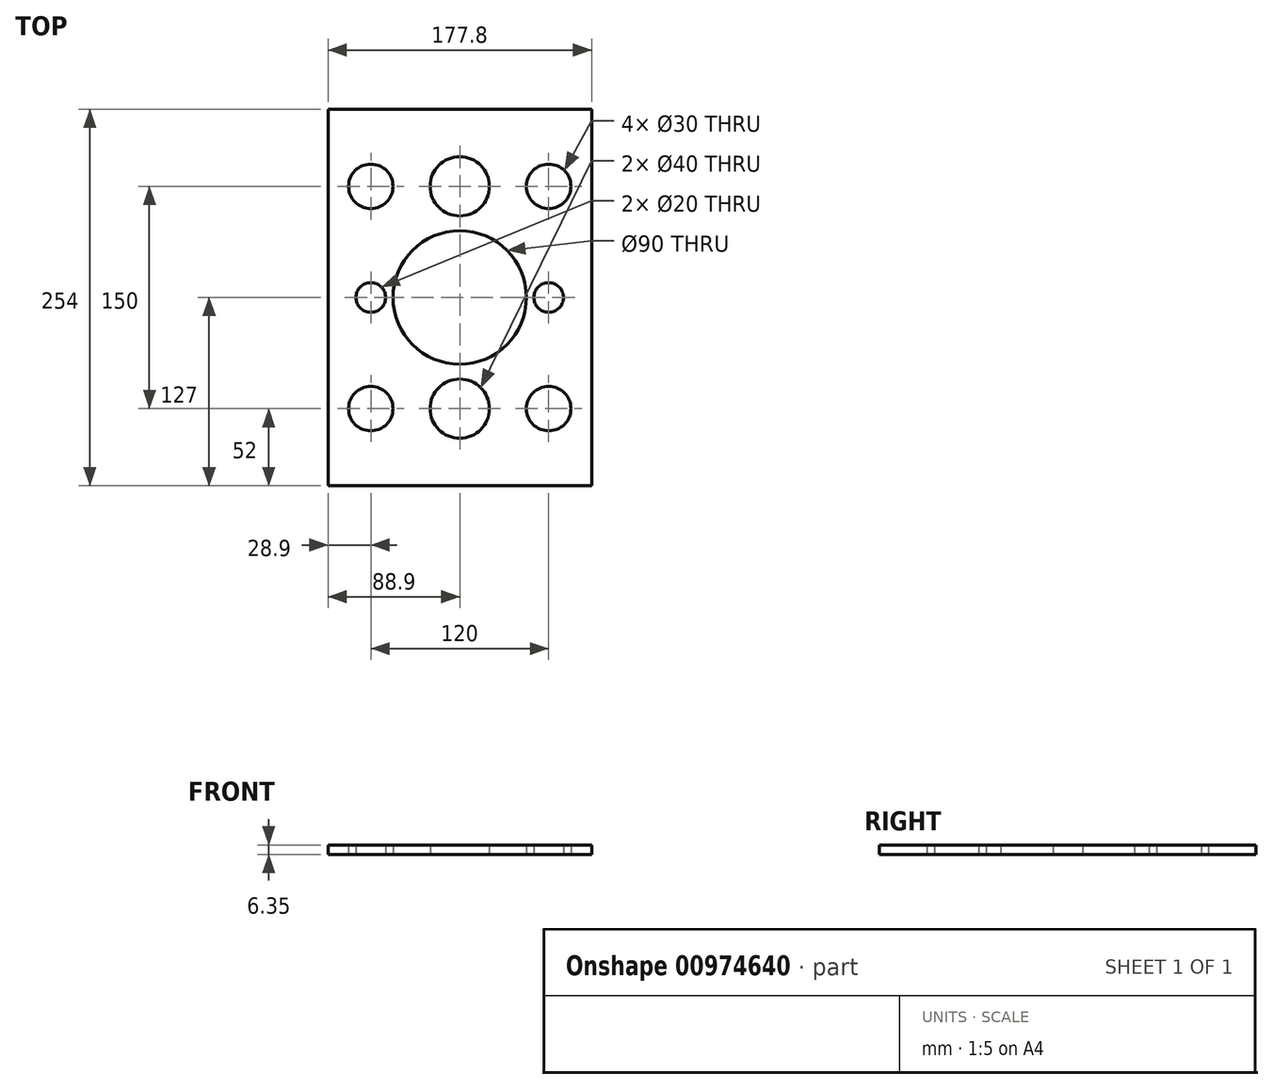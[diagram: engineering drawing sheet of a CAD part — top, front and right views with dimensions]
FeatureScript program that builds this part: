
annotation { "Feature Type Name" : "Feature", "Feature Type Description" : "" }
export const myFeature = defineFeature(function(context is Context, id is Id, definition is map)
    precondition{}
    {
        {
            var Q0;
            Q0=qCreatedBy(makeId("Top.planeOp"),FACE);
            var sketch = newSketch(context, id + "F0", { "sketchPlane" : qUnion([Q0])});
            skLineSegment(sketch, "E0.bottom", {"start": v(88.9, -127) * mm, "end": v(-88.9, -127) * mm});
            skLineSegment(sketch, "E0.top", {"start": v(88.9, 127) * mm, "end": v(-88.9, 127) * mm});
            skLineSegment(sketch, "E0.left", {"start": v(88.9, -127) * mm, "end": v(88.9, 127) * mm});
            skLineSegment(sketch, "E0.right", {"start": v(-88.9, -127) * mm, "end": v(-88.9, 127) * mm});
            skPoint(sketch, "E0.middle", {"position": v(0, 0) * mm});
            skCircle(sketch, "E1", {"center": v(0, 0) * mm, "radius": 45 * mm});
            skCircle(sketch, "E2", {"center": v(0, 75) * mm, "radius": 20 * mm});
            skCircle(sketch, "E3", {"center": v(-60, 75) * mm, "radius": 15 * mm});
            skCircle(sketch, "E4", {"center": v(60, 75) * mm, "radius": 15 * mm});
            skCircle(sketch, "E5.MirrorC", {"center": v(60, -75) * mm, "radius": 15 * mm});
            skCircle(sketch, "E6.MirrorC", {"center": v(-60, -75) * mm, "radius": 15 * mm});
            skCircle(sketch, "E7.MirrorC", {"center": v(0, -75) * mm, "radius": 20 * mm});
            skCircle(sketch, "E8", {"center": v(-60, 0) * mm, "radius": 10 * mm});
            skCircle(sketch, "E9.MirrorC", {"center": v(60, 0) * mm, "radius": 10 * mm});
            skSolve(sketch);
        }
        {
            var Q0;
            Q0=makeQuery(id+"F0.imprint","IMPRINT",FACE,{"disambiguationData":[TD([[makeQuery(id+"F0.imprint","IMPRINT",EDGE,{"derivedFrom":sQuery(id+"F0.wireOp",EDGE,"E0.bottom")}),-1.0]])]});
            extrude(context, id + "F1", {"entities" : qUnion([Q0]), "depth" : 6.35 * mm, "offsetDistance" : 25 * mm});
        }
    });
